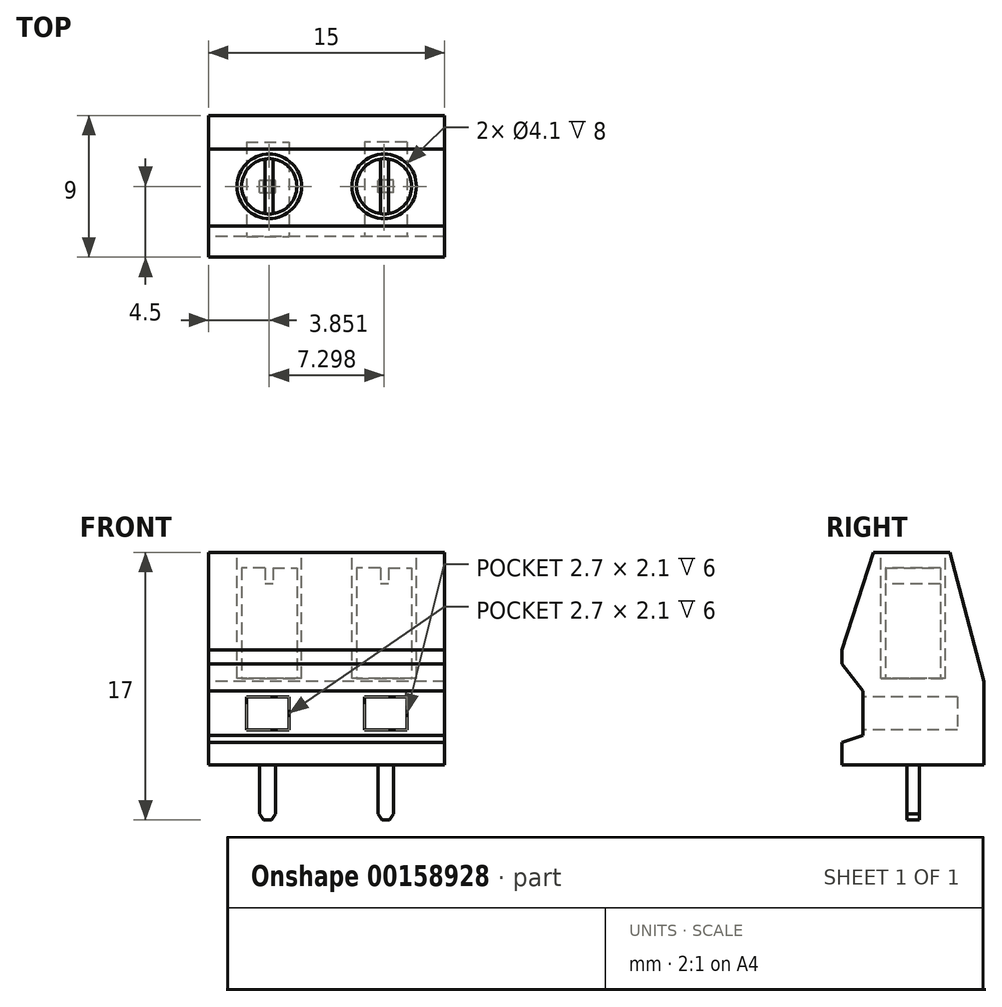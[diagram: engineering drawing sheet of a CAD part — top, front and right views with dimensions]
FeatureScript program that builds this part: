
annotation { "Feature Type Name" : "Feature", "Feature Type Description" : "" }
export const myFeature = defineFeature(function(context is Context, id is Id, definition is map)
    precondition{}
    {
        {
            var Q0;
            Q0=qCreatedBy(makeId("Right.planeOp"),FACE);
            var sketch = newSketch(context, id + "F0", { "sketchPlane" : qUnion([Q0])});
            skLineSegment(sketch, "E0.bottom", {"start": v(-4.5, 0) * mm, "end": v(4.5, 0) * mm});
            skLineSegment(sketch, "E1", {"start": v(-4.5, 7.3) * mm, "end": v(-2.52, 13.5) * mm});
            skLineSegment(sketch, "E2", {"start": v(2.35, 13.5) * mm, "end": v(4.5, 5.3) * mm});
            skLineSegment(sketch, "E3", {"start": v(-4.5, 6.42) * mm, "end": v(-3.2, 4.7) * mm});
            skLineSegment(sketch, "E4", {"start": v(-3.2, 4.7) * mm, "end": v(-3.2, 1.87) * mm});
            skLineSegment(sketch, "E5", {"start": v(-3.2, 1.87) * mm, "end": v(-4.5, 1.43) * mm});
            skLineSegment(sketch, "E6", {"start": v(-2.52, 13.5) * mm, "end": v(2.35, 13.5) * mm});
            skLineSegment(sketch, "E7", {"start": v(-4.5, 7.3) * mm, "end": v(-4.5, 6.42) * mm});
            skLineSegment(sketch, "E8", {"start": v(-4.5, 1.43) * mm, "end": v(-4.5, 0) * mm});
            skLineSegment(sketch, "E9", {"start": v(4.5, 0) * mm, "end": v(4.5, 5.3) * mm});
            skSolve(sketch);
        }
        {
            var Q0;
            Q0 = qSketchRegion(id + "F0", true);
            extrude(context, id + "F1", {"entities" : qUnion([Q0]), "endBound" : BoundingType.SYMMETRIC, "depth" : 15 * mm});
        }
        {
            var Q0;
            Q0=makeQuery(id+"F1.opExtrude","SWEPT_FACE",FACE,{"disambiguationData":[OSD([sQuery(id+"F0.wireOp",EDGE,"E4")])]});
            var sketch = newSketch(context, id + "F2", { "sketchPlane" : qUnion([Q0])});
            skLineSegment(sketch, "E10.bottom", {"start": v(-5.1, 4.33) * mm, "end": v(-2.4, 4.33) * mm});
            skLineSegment(sketch, "E10.top", {"start": v(-5.1, 2.23) * mm, "end": v(-2.4, 2.23) * mm});
            skLineSegment(sketch, "E10.left", {"start": v(-5.1, 4.33) * mm, "end": v(-5.1, 2.23) * mm});
            skLineSegment(sketch, "E10.right", {"start": v(-2.4, 4.33) * mm, "end": v(-2.4, 2.23) * mm});
            skLineSegment(sketch, "E11.MirrorCS", {"start": v(5.1, 4.33) * mm, "end": v(2.4, 4.33) * mm});
            skLineSegment(sketch, "E12.MirrorCS", {"start": v(5.1, 2.23) * mm, "end": v(2.4, 2.23) * mm});
            skLineSegment(sketch, "E13.MirrorCS", {"start": v(2.4, 4.33) * mm, "end": v(2.4, 2.23) * mm});
            skLineSegment(sketch, "E14.MirrorCS", {"start": v(5.1, 4.33) * mm, "end": v(5.1, 2.23) * mm});
            skSolve(sketch);
        }
        {
            var Q0;
            Q0 = qSketchRegion(id + "F2", true);
            extrude(context, id + "F3", {"entities" : qUnion([Q0]), "operationType" : NewBodyOperationType.REMOVE, "oppositeDirection" : true, "depth" : 6 * mm});
        }
        {
            var Q0;
            Q0=makeQuery(id+"F1.opExtrude","SWEPT_FACE",FACE,{"disambiguationData":[OSD([sQuery(id+"F0.wireOp",EDGE,"E6")])]});
            var sketch = newSketch(context, id + "F4", { "sketchPlane" : qUnion([Q0])});
            skCircle(sketch, "E15", {"center": v(-3.65, 0) * mm, "radius": 2.05 * mm});
            skCircle(sketch, "E16.MirrorC", {"center": v(3.65, 0) * mm, "radius": 2.05 * mm});
            skSolve(sketch);
        }
        {
            var Q0;
            Q0 = qSketchRegion(id + "F4", true);
            extrude(context, id + "F5", {"entities" : qUnion([Q0]), "operationType" : NewBodyOperationType.REMOVE, "oppositeDirection" : true, "depth" : 8 * mm});
        }
        {
            var Q0;
            Q0=makeQuery(id+"F5.boolean.opBoolean","COPY",FACE,{"derivedFrom":makeQuery(id+"F5.opExtrude","CAP_FACE",FACE,{"disambiguationData":[OSD([sQuery(id+"F4.wireOp",EDGE,"E16.MirrorC")])],"isStart":false})});
            var sketch = newSketch(context, id + "F6", { "sketchPlane" : qUnion([Q0])});
            skCircle(sketch, "E17", {"center": v(3.65, 0) * mm, "radius": 1.75 * mm});
            skCircle(sketch, "E18.MirrorC", {"center": v(-3.65, 0) * mm, "radius": 1.75 * mm});
            skSolve(sketch);
        }
        {
            var Q0;
            Q0 = qSketchRegion(id + "F6", true);
            extrude(context, id + "F7", {"entities" : qUnion([Q0]), "depth" : 7 * mm});
        }
        {
            var Q0;
            Q0=makeQuery(id+"F7.opExtrude","CAP_FACE",FACE,{"disambiguationData":[OSD([sQuery(id+"F6.wireOp",EDGE,"E18.MirrorC")])],"isStart":false});
            var sketch = newSketch(context, id + "F8", { "sketchPlane" : qUnion([Q0])});
            skLineSegment(sketch, "E19.bottom", {"start": v(-3.92, 1.87) * mm, "end": v(-3.42, 1.87) * mm});
            skLineSegment(sketch, "E19.top", {"start": v(-3.92, -1.9) * mm, "end": v(-3.42, -1.9) * mm});
            skLineSegment(sketch, "E19.left", {"start": v(-3.92, 1.87) * mm, "end": v(-3.92, -1.9) * mm});
            skLineSegment(sketch, "E19.right", {"start": v(-3.42, 1.87) * mm, "end": v(-3.42, -1.9) * mm});
            skLineSegment(sketch, "E20.MirrorCS", {"start": v(3.92, 1.87) * mm, "end": v(3.42, 1.87) * mm});
            skLineSegment(sketch, "E21.MirrorCS", {"start": v(3.92, -1.9) * mm, "end": v(3.42, -1.9) * mm});
            skLineSegment(sketch, "E22.MirrorCS", {"start": v(3.42, 1.87) * mm, "end": v(3.42, -1.9) * mm});
            skLineSegment(sketch, "E23.MirrorCS", {"start": v(3.92, 1.87) * mm, "end": v(3.92, -1.9) * mm});
            skSolve(sketch);
        }
        {
            var Q0;
            Q0 = qSketchRegion(id + "F8", true);
            extrude(context, id + "F9", {"entities" : qUnion([Q0]), "operationType" : NewBodyOperationType.REMOVE, "oppositeDirection" : true, "depth" : 1 * mm});
        }
        {
            var Q0;
            Q0=qCreatedBy(makeId("Front.planeOp"),FACE);
            var sketch = newSketch(context, id + "F10", { "sketchPlane" : qUnion([Q0])});
            skLineSegment(sketch, "E24.bottom", {"start": v(-4.25, 0) * mm, "end": v(-3.25, 0) * mm});
            skLineSegment(sketch, "E25", {"start": v(-4.25, -3.11) * mm, "end": v(-4, -3.5) * mm});
            skLineSegment(sketch, "E26", {"start": v(-4, -3.5) * mm, "end": v(-3.5, -3.5) * mm});
            skLineSegment(sketch, "E27", {"start": v(-3.5, -3.5) * mm, "end": v(-3.25, -3.11) * mm});
            skLineSegment(sketch, "E28", {"start": v(-4.25, 0) * mm, "end": v(-4.25, -3.11) * mm});
            skLineSegment(sketch, "E29", {"start": v(-3.25, -3.11) * mm, "end": v(-3.25, 0) * mm});
            skLineSegment(sketch, "E30.MirrorCS", {"start": v(3.5, -3.5) * mm, "end": v(3.25, -3.11) * mm});
            skLineSegment(sketch, "E31.MirrorCS", {"start": v(4, -3.5) * mm, "end": v(3.5, -3.5) * mm});
            skLineSegment(sketch, "E32.MirrorCS", {"start": v(4.25, -3.11) * mm, "end": v(4, -3.5) * mm});
            skLineSegment(sketch, "E33.MirrorCS", {"start": v(4.25, 0) * mm, "end": v(4.25, -3.11) * mm});
            skLineSegment(sketch, "E34.MirrorCS", {"start": v(3.25, -3.11) * mm, "end": v(3.25, 0) * mm});
            skLineSegment(sketch, "E35.MirrorCS", {"start": v(4.25, 0) * mm, "end": v(3.25, 0) * mm});
            skSolve(sketch);
        }
        {
            var Q0;
            Q0 = qSketchRegion(id + "F10", true);
            extrude(context, id + "F11", {"entities" : qUnion([Q0]), "endBound" : BoundingType.SYMMETRIC, "depth" : .8 * mm});
        }
    });
